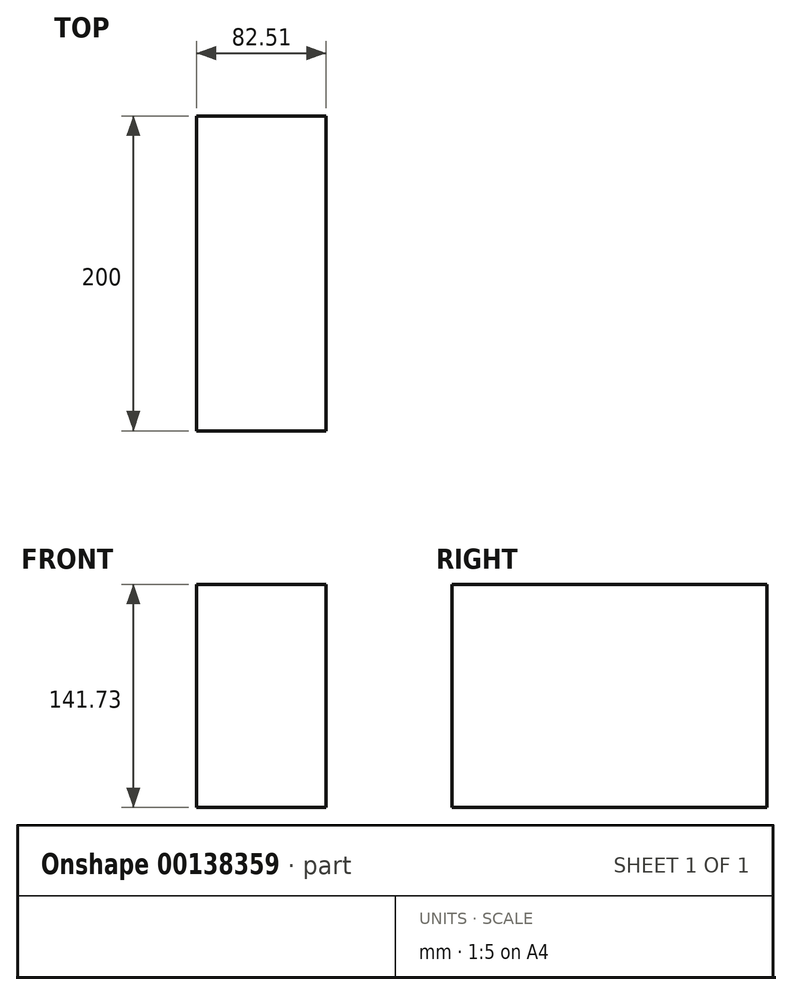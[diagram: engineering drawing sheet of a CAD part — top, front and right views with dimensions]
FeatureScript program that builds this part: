
annotation { "Feature Type Name" : "Feature", "Feature Type Description" : "" }
export const myFeature = defineFeature(function(context is Context, id is Id, definition is map)
    precondition{}
    {
        {
            var Q0;
            Q0=qCreatedBy(makeId("Top.planeOp"),FACE);
            var sketch = newSketch(context, id + "F0", { "sketchPlane" : qUnion([Q0])});
            skLineSegment(sketch, "E0.bottom", {"start": v(1.85, 98.35) * mm, "end": v(84.36, 98.35) * mm});
            skLineSegment(sketch, "E0.top", {"start": v(1.85, -101.65) * mm, "end": v(84.36, -101.65) * mm});
            skLineSegment(sketch, "E0.left", {"start": v(1.85, 98.35) * mm, "end": v(1.85, -101.65) * mm});
            skLineSegment(sketch, "E0.right", {"start": v(84.36, 98.35) * mm, "end": v(84.36, -101.65) * mm});
            skSolve(sketch);
        }
        {
            var Q0;
            Q0 = qSketchRegion(id + "F0", true);
            var Q1;
            Q1=sQuery(id+"F0.wireOp",EDGE,"E0.top");
            var Q2;
            Q2=sQuery(id+"F0.wireOp",EDGE,"E0.left");
            var Q3;
            Q3=sQuery(id+"F0.wireOp",EDGE,"E0.bottom");
            var Q4;
            Q4=sQuery(id+"F0.wireOp",EDGE,"E0.right");
            extrude(context, id + "F1", {"entities" : qUnion([Q0]), "bodyType" : ToolBodyType.SURFACE, "surfaceEntities" : qUnion([Q1, Q2, Q3, Q4]), "depth" : 141.73 * mm});
        }
    });
